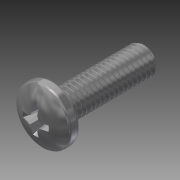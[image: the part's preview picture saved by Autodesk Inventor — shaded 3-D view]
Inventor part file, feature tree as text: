
AUTODESK INVENTOR PART (.ipt)
format: ipt  version: 2014 SP1 (Build 180222100, 222)  size: 750,080 bytes
history: native  units: in
note: dims shown in document units (in); Inventor stores cm internally (conversion verified against a paired STEP export)
features: fillet x1, other x1, imported_body x1
ambient origin geometry x8: Origin, YZ Plane, XZ Plane, XY Plane, X Axis, Y Axis, Z Axis, Center Point
bodies: Body1 (feature_tree)
feature tree (3):
  fillet  "Fillet1"  [1 undecoded]
  other  "91735A8301"
  imported_body  "Base1"
note: 1 required parameter value undecoded (feature->parameter linkage not recoverable at this tier; creation-order binding heuristic only, values carry confidence <= 0.55)
